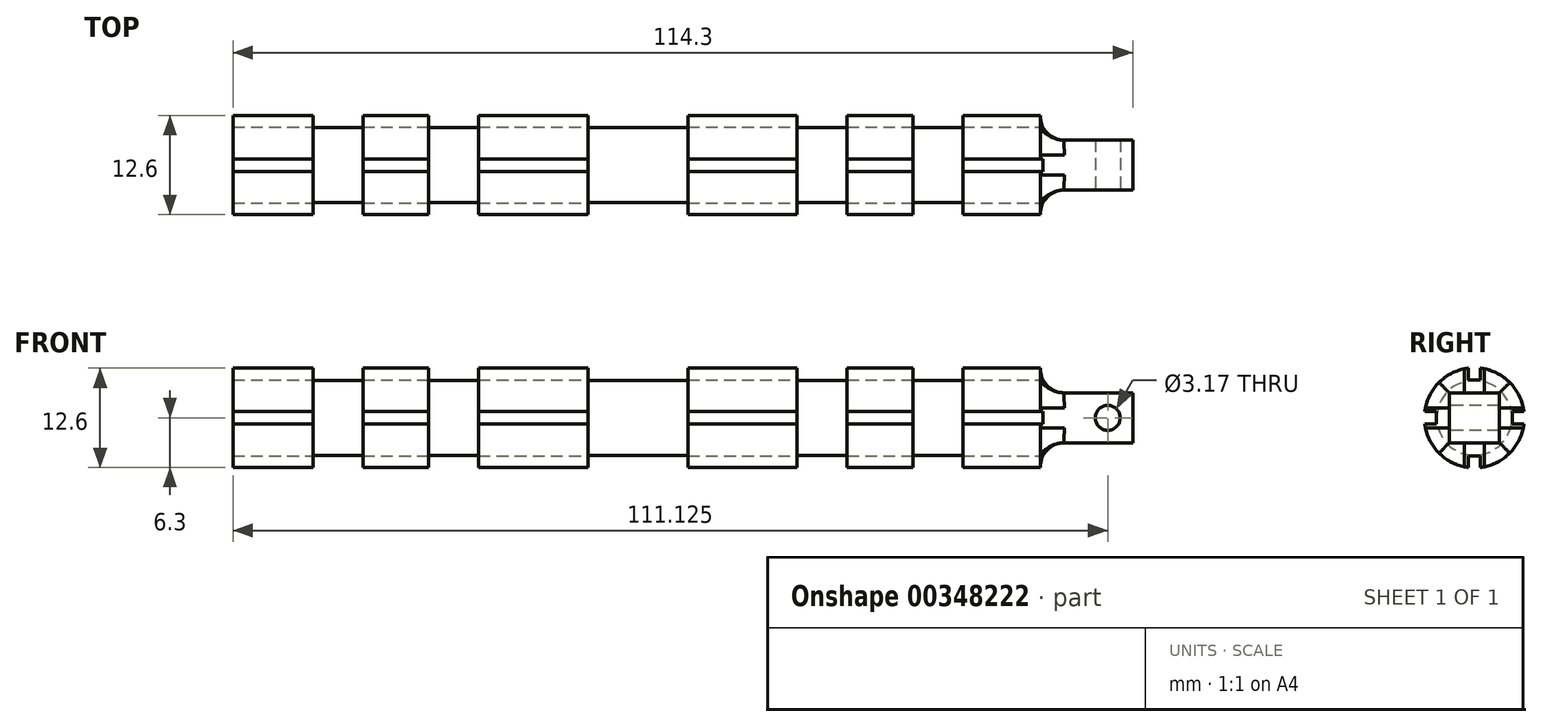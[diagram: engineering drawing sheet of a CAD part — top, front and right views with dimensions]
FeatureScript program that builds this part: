
annotation { "Feature Type Name" : "Feature", "Feature Type Description" : "" }
export const myFeature = defineFeature(function(context is Context, id is Id, definition is map)
    precondition{}
    {
        {
            var Q0;
            Q0=qCreatedBy(makeId("Front.planeOp"),FACE);
            var sketch = newSketch(context, id + "F0", { "sketchPlane" : qUnion([Q0])});
            skLineSegment(sketch, "E0", {"start": v(-57.15, 0) * mm, "end": v(57.15, 0) * mm});
            skLineSegment(sketch, "E1", {"start": v(57.15, 0) * mm, "end": v(57.15, 4.76) * mm});
            skLineSegment(sketch, "E2", {"start": v(45.4, 6.35) * mm, "end": v(35.56, 6.35) * mm});
            skLineSegment(sketch, "E3", {"start": v(35.56, 6.35) * mm, "end": v(35.56, 4.76) * mm});
            skLineSegment(sketch, "E4", {"start": v(35.56, 4.76) * mm, "end": v(29.21, 4.76) * mm});
            skLineSegment(sketch, "E5", {"start": v(29.21, 4.76) * mm, "end": v(29.21, 6.35) * mm});
            skLineSegment(sketch, "E6", {"start": v(29.21, 6.35) * mm, "end": v(20.88, 6.35) * mm});
            skLineSegment(sketch, "E7", {"start": v(20.88, 6.35) * mm, "end": v(20.88, 4.76) * mm});
            skLineSegment(sketch, "E8", {"start": v(20.88, 4.76) * mm, "end": v(14.53, 4.76) * mm});
            skLineSegment(sketch, "E9", {"start": v(14.53, 4.76) * mm, "end": v(14.53, 6.35) * mm});
            skLineSegment(sketch, "E10", {"start": v(14.53, 6.35) * mm, "end": v(0.63, 6.35) * mm});
            skLineSegment(sketch, "E11", {"start": v(0.63, 6.35) * mm, "end": v(0.63, 4.76) * mm});
            skLineSegment(sketch, "E12", {"start": v(0.63, 4.76) * mm, "end": v(-12.07, 4.76) * mm});
            skLineSegment(sketch, "E13", {"start": v(-12.07, 4.76) * mm, "end": v(-12.07, 6.35) * mm});
            skLineSegment(sketch, "E14", {"start": v(-12.07, 6.35) * mm, "end": v(-25.96, 6.35) * mm});
            skLineSegment(sketch, "E15", {"start": v(-25.96, 6.35) * mm, "end": v(-25.96, 4.76) * mm});
            skLineSegment(sketch, "E16", {"start": v(-25.96, 4.76) * mm, "end": v(-32.3, 4.76) * mm});
            skLineSegment(sketch, "E17", {"start": v(-32.3, 4.76) * mm, "end": v(-32.3, 6.35) * mm});
            skLineSegment(sketch, "E18", {"start": v(-32.3, 6.35) * mm, "end": v(-40.64, 6.35) * mm});
            skLineSegment(sketch, "E19", {"start": v(-40.64, 6.35) * mm, "end": v(-40.64, 4.76) * mm});
            skLineSegment(sketch, "E20", {"start": v(-40.64, 4.76) * mm, "end": v(-47, 4.76) * mm});
            skLineSegment(sketch, "E21", {"start": v(-47, 4.76) * mm, "end": v(-47, 6.35) * mm});
            skLineSegment(sketch, "E22", {"start": v(-47, 6.35) * mm, "end": v(-57.15, 6.35) * mm});
            skLineSegment(sketch, "E23", {"start": v(-57.15, 6.35) * mm, "end": v(-57.15, 0) * mm});
            skLineSegment(sketch, "E24", {"start": v(45.4, 6.35) * mm, "end": v(45.4, 4.76) * mm});
            skLineSegment(sketch, "E25", {"start": v(57.15, 4.76) * mm, "end": v(45.4, 4.76) * mm});
            skSolve(sketch);
        }
        {
            var Q0;
            Q0=qSketchRegion(id+"F0",true);
            var Q1;
            Q1=sQuery(id+"F0.wireOp",EDGE,"E0");
            revolve(context, id + "F1", {"entities" : qUnion([Q0]), "axis" : qUnion([Q1]), "revolveType" : RevolveType.FULL});
        }
        {
            var Q0;
            Q0=makeQuery(id+"F1.opRevolve","SWEPT_FACE",FACE,{"disambiguationData":[OSD([sQuery(id+"F0.wireOp",EDGE,"E1")])]});
            var sketch = newSketch(context, id + "F2", { "sketchPlane" : qUnion([Q0])});
            skCircle(sketch, "E26.0", {"center": v(0, 0) * mm, "radius": 4.76 * mm});
            skLineSegment(sketch, "E27.rect.bottom", {"start": v(-3.17, 3.18) * mm, "end": v(3.18, 3.18) * mm});
            skLineSegment(sketch, "E27.rect.top", {"start": v(-3.18, -3.18) * mm, "end": v(3.17, -3.18) * mm});
            skLineSegment(sketch, "E27.rect.left", {"start": v(-3.17, 3.18) * mm, "end": v(-3.18, -3.17) * mm});
            skLineSegment(sketch, "E27.rect.right", {"start": v(3.18, 3.18) * mm, "end": v(3.17, -3.18) * mm});
            skSolve(sketch);
        }
        {
            var Q0;
            Q0=qSketchRegion(id+"F2",true);
            extrude(context, id + "F3", {"entities" : qUnion([Q0]), "operationType" : NewBodyOperationType.REMOVE, "oppositeDirection" : true, "depth" : 11.75 * mm});
        }
        {
            var Q0;
            Q0=makeQuery(id+"F3.boolean.opBoolean","COPY",FACE,{"derivedFrom":makeQuery(id+"F3.opExtrude","SWEPT_FACE",FACE,{"disambiguationData":[OSD([sQuery(id+"F2.wireOp",EDGE,"E27.rect.left")])]})});
            var sketch = newSketch(context, id + "F4", { "sketchPlane" : qUnion([Q0])});
            skPoint(sketch, "E28", {"position": v(53.98, 0) * mm});
            skSolve(sketch);
        }
        {
            var Q0;
            Q0=sQuery(id+"F4.wireOp",VERTEX,"E28");
            var Q1;
            Q1=makeQuery(id+"F1.opRevolve","SWEPT_BODY",BODY,{"disambiguationData":[OSD([sQuery(id+"F0.wireOp",EDGE,"E0"),sQuery(id+"F0.wireOp",EDGE,"E1"),sQuery(id+"F0.wireOp",EDGE,"E2"),sQuery(id+"F0.wireOp",EDGE,"E3"),sQuery(id+"F0.wireOp",EDGE,"E4"),sQuery(id+"F0.wireOp",EDGE,"E5"),sQuery(id+"F0.wireOp",EDGE,"E6"),sQuery(id+"F0.wireOp",EDGE,"E7"),sQuery(id+"F0.wireOp",EDGE,"E8"),sQuery(id+"F0.wireOp",EDGE,"E9"),sQuery(id+"F0.wireOp",EDGE,"E10"),sQuery(id+"F0.wireOp",EDGE,"E11"),sQuery(id+"F0.wireOp",EDGE,"E12"),sQuery(id+"F0.wireOp",EDGE,"E13"),sQuery(id+"F0.wireOp",EDGE,"E14"),sQuery(id+"F0.wireOp",EDGE,"E15"),sQuery(id+"F0.wireOp",EDGE,"E16"),sQuery(id+"F0.wireOp",EDGE,"E17"),sQuery(id+"F0.wireOp",EDGE,"E18"),sQuery(id+"F0.wireOp",EDGE,"E19"),sQuery(id+"F0.wireOp",EDGE,"E20"),sQuery(id+"F0.wireOp",EDGE,"E21"),sQuery(id+"F0.wireOp",EDGE,"E22"),sQuery(id+"F0.wireOp",EDGE,"E23"),sQuery(id+"F0.wireOp",EDGE,"E24"),sQuery(id+"F0.wireOp",EDGE,"E25")])]});
            hole(context, id + "F5", {"style" : HoleStyle.SIMPLE, "holeDiameter" : 3.17 * mm, "endStyle" : HoleEndStyle.THROUGH, "locations" : qUnion([Q0]), "scope" : qUnion([Q1])});
        }
        {
            var Q0;
            Q0=makeQuery(id+"F3.boolean.opBoolean","COPY",EDGE,{"derivedFrom":makeQuery(id+"F3.opExtrude","CAP_EDGE",EDGE,{"disambiguationData":[OSD([sQuery(id+"F2.wireOp",EDGE,"E27.rect.bottom")])],"isStart":false})});
            var Q1;
            Q1=makeQuery(id+"F3.boolean.opBoolean","COPY",EDGE,{"derivedFrom":makeQuery(id+"F3.opExtrude","CAP_EDGE",EDGE,{"disambiguationData":[OSD([sQuery(id+"F2.wireOp",EDGE,"E27.rect.left")])],"isStart":false})});
            var Q2;
            Q2=makeQuery(id+"F3.boolean.opBoolean","COPY",EDGE,{"derivedFrom":makeQuery(id+"F3.opExtrude","CAP_EDGE",EDGE,{"disambiguationData":[OSD([sQuery(id+"F2.wireOp",EDGE,"E27.rect.top")])],"isStart":false})});
            var Q3;
            Q3=makeQuery(id+"F3.boolean.opBoolean","COPY",EDGE,{"derivedFrom":makeQuery(id+"F3.opExtrude","CAP_EDGE",EDGE,{"disambiguationData":[OSD([sQuery(id+"F2.wireOp",EDGE,"E27.rect.right")])],"isStart":false})});
            fillet(context, id + "F6", {"entities" : qUnion([Q0, Q1, Q2, Q3]), "radius" : 3.05 * mm, "tangentPropagation" : true, "allowEdgeOverflow" : false});
        }
        {
            var Q0;
            Q0=qCreatedBy(makeId("Right.planeOp"),FACE);
            var sketch = newSketch(context, id + "F7", { "sketchPlane" : qUnion([Q0])});
            skLineSegment(sketch, "E29.rect.bottom", {"start": v(-0.79, 6.35) * mm, "end": v(0.79, 6.35) * mm});
            skLineSegment(sketch, "E29.rect.top", {"start": v(-0.79, 4.83) * mm, "end": v(0.79, 4.83) * mm});
            skLineSegment(sketch, "E29.rect.left", {"start": v(-0.79, 6.35) * mm, "end": v(-0.79, 4.83) * mm});
            skLineSegment(sketch, "E29.rect.right", {"start": v(0.79, 6.35) * mm, "end": v(0.79, 4.83) * mm});
            skPoint(sketch, "E29.rect.middle", {"position": v(0, 5.59) * mm});
            skLineSegment(sketch, "E30.rect.bottom", {"start": v(-4.83, -0.79) * mm, "end": v(-6.35, -0.79) * mm});
            skLineSegment(sketch, "E30.rect.top", {"start": v(-4.83, 0.79) * mm, "end": v(-6.35, 0.79) * mm});
            skLineSegment(sketch, "E30.rect.left", {"start": v(-4.83, -0.79) * mm, "end": v(-4.83, 0.79) * mm});
            skLineSegment(sketch, "E30.rect.right", {"start": v(-6.35, -0.79) * mm, "end": v(-6.35, 0.79) * mm});
            skPoint(sketch, "E30.rect.middle", {"position": v(-5.59, 0) * mm});
            skLineSegment(sketch, "E31.rect.bottom", {"start": v(6.35, -0.79) * mm, "end": v(4.83, -0.79) * mm});
            skLineSegment(sketch, "E31.rect.top", {"start": v(6.35, 0.79) * mm, "end": v(4.83, 0.79) * mm});
            skLineSegment(sketch, "E31.rect.left", {"start": v(6.35, -0.79) * mm, "end": v(6.35, 0.79) * mm});
            skLineSegment(sketch, "E31.rect.right", {"start": v(4.83, -0.79) * mm, "end": v(4.83, 0.79) * mm});
            skPoint(sketch, "E31.rect.middle", {"position": v(5.59, 0) * mm});
            skLineSegment(sketch, "E32.rect.bottom", {"start": v(0.79, -6.35) * mm, "end": v(-0.79, -6.35) * mm});
            skLineSegment(sketch, "E32.rect.top", {"start": v(0.79, -4.83) * mm, "end": v(-0.79, -4.83) * mm});
            skLineSegment(sketch, "E32.rect.left", {"start": v(0.79, -6.35) * mm, "end": v(0.79, -4.83) * mm});
            skLineSegment(sketch, "E32.rect.right", {"start": v(-0.79, -6.35) * mm, "end": v(-0.79, -4.83) * mm});
            skPoint(sketch, "E32.rect.middle", {"position": v(0, -5.59) * mm});
            skSolve(sketch);
        }
        {
            var Q0;
            Q0=qSketchRegion(id+"F7",true);
            extrude(context, id + "F8", {"entities" : qUnion([Q0]), "operationType" : NewBodyOperationType.REMOVE, "endBound" : BoundingType.SYMMETRIC, "oppositeDirection" : true, "depth" : 127 * mm});
        }
    });
